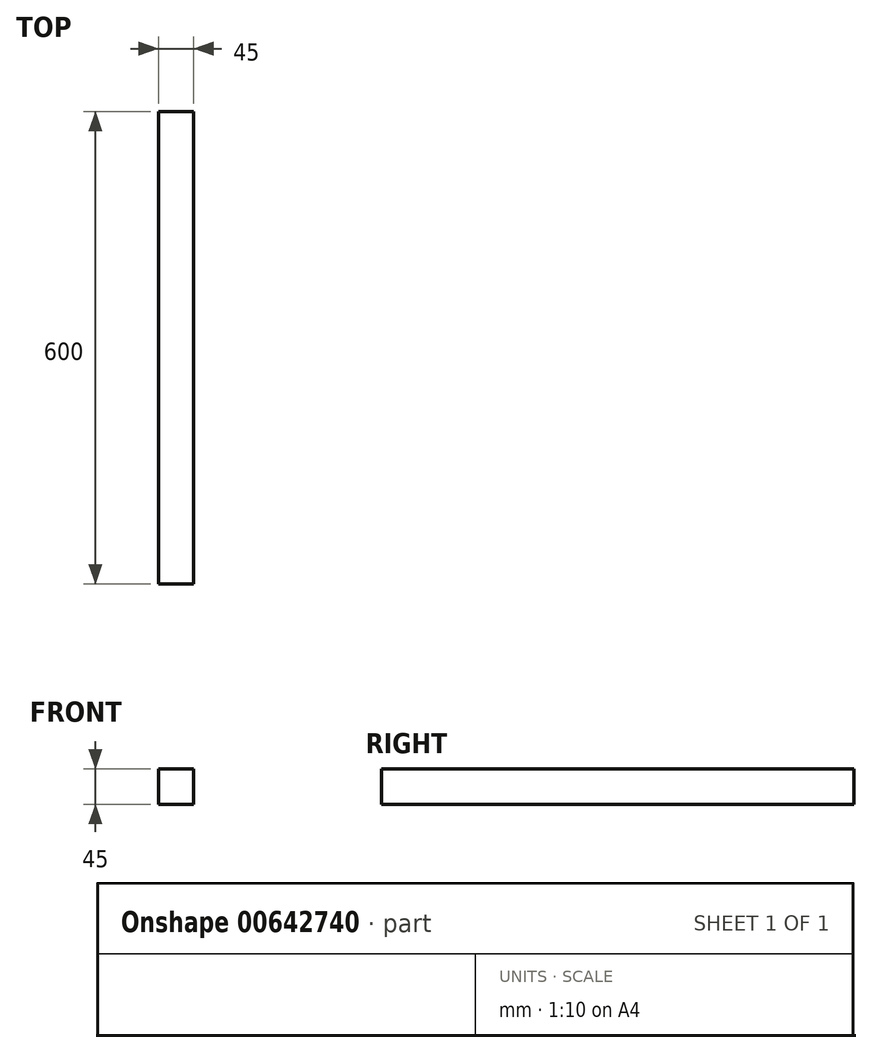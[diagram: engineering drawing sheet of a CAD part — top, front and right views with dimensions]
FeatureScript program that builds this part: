
annotation { "Feature Type Name" : "Feature", "Feature Type Description" : "" }
export const myFeature = defineFeature(function(context is Context, id is Id, definition is map)
    precondition{}
    {
        {
            var Q0;
            Q0=qCreatedBy(makeId("Front.planeOp"),FACE);
            var sketch = newSketch(context, id + "F0", { "sketchPlane" : qUnion([Q0])});
            skLineSegment(sketch, "E0.bottom", {"start": v(0, 0) * mm, "end": v(45, 0) * mm});
            skLineSegment(sketch, "E0.top", {"start": v(0, 45) * mm, "end": v(45, 45) * mm});
            skLineSegment(sketch, "E0.left", {"start": v(0, 0) * mm, "end": v(0, 45) * mm});
            skLineSegment(sketch, "E0.right", {"start": v(45, 0) * mm, "end": v(45, 45) * mm});
            skSolve(sketch);
        }
        {
            var Q0;
            Q0 = qSketchRegion(id + "F0", true);
            extrude(context, id + "F1", {"entities" : qUnion([Q0]), "depth" : 600 * mm, "offsetDistance" : 25 * mm});
        }
    });
